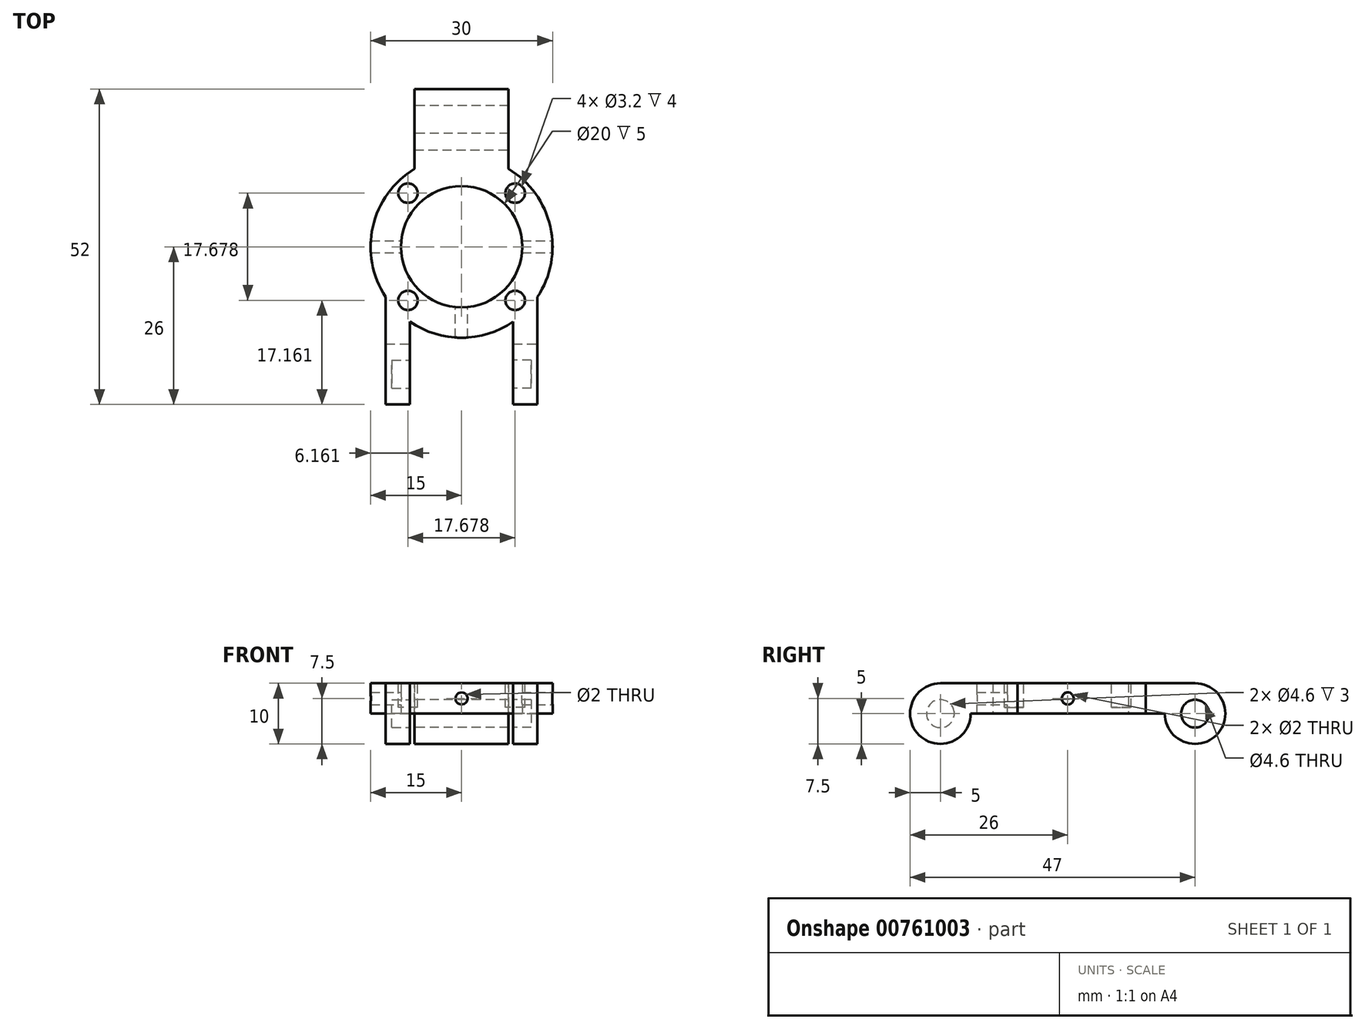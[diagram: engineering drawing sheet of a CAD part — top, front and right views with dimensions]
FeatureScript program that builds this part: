
annotation { "Feature Type Name" : "Feature", "Feature Type Description" : "" }
export const myFeature = defineFeature(function(context is Context, id is Id, definition is map)
    precondition{}
    {
        {
            var Q0;
            Q0=qCreatedBy(makeId("Top.planeOp"),FACE);
            var sketch = newSketch(context, id + "F0", { "sketchPlane" : qUnion([Q0])});
            skCircle(sketch, "E0", {"center": v(0, 0) * mm, "radius": 10 * mm});
            skArc(sketch, "E1", {"start": v(-7.75, 12.84) * mm, "mid": v(-15, 0.45) * mm, "end": v(-8.5, -12.36) * mm});
            skLineSegment(sketch, "E2", {"start": v(-7.75, 26) * mm, "end": v(-7.75, 12.84) * mm});
            skLineSegment(sketch, "E3", {"start": v(7.75, 26) * mm, "end": v(7.75, 12.84) * mm});
            skLineSegment(sketch, "E4", {"start": v(-7.75, 26) * mm, "end": v(7.75, 26) * mm});
            skLineSegment(sketch, "E5", {"start": v(-8.5, -12.36) * mm, "end": v(-8.5, -26) * mm});
            skLineSegment(sketch, "E6", {"start": v(8.5, -26) * mm, "end": v(8.5, -12.36) * mm});
            skArc(sketch, "E7.trimOffspring", {"start": v(8.5, -12.36) * mm, "mid": v(15, 0.45) * mm, "end": v(7.75, 12.84) * mm});
            skLineSegment(sketch, "E8", {"start": v(8.5, -26) * mm, "end": v(12.5, -26) * mm});
            skLineSegment(sketch, "E9", {"start": v(12.5, -26) * mm, "end": v(12.5, -8.3) * mm});
            skLineSegment(sketch, "E10", {"start": v(-8.5, -26) * mm, "end": v(-12.5, -26) * mm});
            skLineSegment(sketch, "E11", {"start": v(-12.5, -26) * mm, "end": v(-12.5, -8.3) * mm});
            skCircle(sketch, "E12", {"center": v(0, 0) * mm, "radius": 15 * mm});
            skPoint(sketch, "E13.orphan", {"position": v(7.75, 6.32) * mm});
            skSolve(sketch);
        }
        {
            var Q0;
            Q0 = qSketchRegion(id + "F0", true);
            extrude(context, id + "F1", {"entities" : qUnion([Q0]), "depth" : 5 * mm, "offsetDistance" : 25 * mm});
        }
        {
            var Q0;
            Q0=makeQuery(id+"F1.opExtrude","CAP_FACE",FACE,{"disambiguationData":[OSD([sQuery(id+"F0.wireOp",EDGE,"E0"),sQuery(id+"F0.wireOp",EDGE,"E1"),sQuery(id+"F0.wireOp",EDGE,"E2"),sQuery(id+"F0.wireOp",EDGE,"E3"),sQuery(id+"F0.wireOp",EDGE,"E4")])],"isStart":true});
            var sketch = newSketch(context, id + "F2", { "sketchPlane" : qUnion([Q0])});
            skLineSegment(sketch, "E14.0", {"start": v(7.75, -26) * mm, "end": v(7.75, -16) * mm});
            skLineSegment(sketch, "E14.1", {"start": v(-7.75, -26) * mm, "end": v(7.75, -26) * mm});
            skLineSegment(sketch, "E14.2", {"start": v(-7.75, -26) * mm, "end": v(-7.75, -16) * mm});
            skLineSegment(sketch, "E15", {"start": v(-7.75, -16) * mm, "end": v(7.75, -16) * mm});
            skLineSegment(sketch, "E16.bottom", {"start": v(-12.5, 26) * mm, "end": v(-8.5, 26) * mm});
            skLineSegment(sketch, "E16.top", {"start": v(-12.5, 16) * mm, "end": v(-8.5, 16) * mm});
            skLineSegment(sketch, "E16.left", {"start": v(-12.5, 26) * mm, "end": v(-12.5, 16) * mm});
            skLineSegment(sketch, "E16.right", {"start": v(-8.5, 26) * mm, "end": v(-8.5, 16) * mm});
            skLineSegment(sketch, "E17.bottom", {"start": v(8.5, 26) * mm, "end": v(12.5, 26) * mm});
            skLineSegment(sketch, "E17.top", {"start": v(8.5, 16) * mm, "end": v(12.5, 16) * mm});
            skLineSegment(sketch, "E17.left", {"start": v(8.5, 26) * mm, "end": v(8.5, 16) * mm});
            skLineSegment(sketch, "E17.right", {"start": v(12.5, 26) * mm, "end": v(12.5, 16) * mm});
            skSolve(sketch);
        }
        {
            var Q0;
            Q0 = qSketchRegion(id + "F2", true);
            extrude(context, id + "F3", {"entities" : qUnion([Q0]), "operationType" : NewBodyOperationType.ADD, "depth" : 5 * mm, "offsetDistance" : 25 * mm});
        }
        {
            var Q0;
            Q0=makeQuery(id+"F3.boolean.opBoolean","MERGE",FACE,{"derivedFrom":[makeQuery(id+"F1.opExtrude","SWEPT_FACE",FACE,{"disambiguationData":[OSD([sQuery(id+"F0.wireOp",EDGE,"E2")])]}),makeQuery(id+"F3.opExtrude","SWEPT_FACE",FACE,{"disambiguationData":[OSD([sQuery(id+"F2.wireOp",EDGE,"E14.2")])]})]});
            var sketch = newSketch(context, id + "F4", { "sketchPlane" : qUnion([Q0])});
            skCircle(sketch, "E18", {"center": v(-21, 0) * mm, "radius": 2.3 * mm});
            skSolve(sketch);
        }
        {
            var Q0;
            Q0 = qSketchRegion(id + "F4", true);
            extrude(context, id + "F5", {"entities" : qUnion([Q0]), "operationType" : NewBodyOperationType.REMOVE, "endBound" : BoundingType.THROUGH_ALL, "oppositeDirection" : true, "depth" : 25 * mm, "offsetDistance" : 25 * mm});
        }
        {
            var Q0;
            Q0=makeQuery(id+"F1.opExtrude","CAP_FACE",FACE,{"disambiguationData":[OSD([sQuery(id+"F0.wireOp",EDGE,"E0"),sQuery(id+"F0.wireOp",EDGE,"E1"),sQuery(id+"F0.wireOp",EDGE,"E2"),sQuery(id+"F0.wireOp",EDGE,"E3"),sQuery(id+"F0.wireOp",EDGE,"E4")])],"isStart":false});
            var sketch = newSketch(context, id + "F6", { "sketchPlane" : qUnion([Q0])});
            skLineSegment(sketch, "E19", {"start": v(0, 0) * mm, "end": v(21.62, -21.62) * mm});
            skLineSegment(sketch, "E20", {"start": v(0, 0) * mm, "end": v(22.98, 22.98) * mm});
            skLineSegment(sketch, "E21", {"start": v(0, 0) * mm, "end": v(-21.47, 21.47) * mm});
            skLineSegment(sketch, "E22", {"start": v(0, 0) * mm, "end": v(-23.27, -23.27) * mm});
            skCircle(sketch, "E23", {"center": v(8.84, 8.84) * mm, "radius": 1.6 * mm});
            skCircle(sketch, "E24", {"center": v(8.84, -8.84) * mm, "radius": 1.6 * mm});
            skCircle(sketch, "E25", {"center": v(-8.84, -8.84) * mm, "radius": 1.6 * mm});
            skCircle(sketch, "E26", {"center": v(-8.84, 8.84) * mm, "radius": 1.6 * mm});
            skSolve(sketch);
        }
        {
            var Q0;
            Q0 = qSketchRegion(id + "F6", true);
            extrude(context, id + "F7", {"entities" : qUnion([Q0]), "operationType" : NewBodyOperationType.REMOVE, "oppositeDirection" : true, "depth" : 4 * mm, "offsetDistance" : 25 * mm});
        }
        {
            var Q0;
            Q0=makeQuery(id+"F3.boolean.opBoolean","MERGE",FACE,{"derivedFrom":[makeQuery(id+"F1.opExtrude","SWEPT_FACE",FACE,{"disambiguationData":[OSD([sQuery(id+"F0.wireOp",EDGE,"E5")])]}),makeQuery(id+"F3.opExtrude","SWEPT_FACE",FACE,{"disambiguationData":[OSD([sQuery(id+"F2.wireOp",EDGE,"E16.right")])]})]});
            var sketch = newSketch(context, id + "F8", { "sketchPlane" : qUnion([Q0])});
            skCircle(sketch, "E27", {"center": v(-21, 0) * mm, "radius": 2.3 * mm});
            skSolve(sketch);
        }
        {
            var Q0;
            Q0 = qSketchRegion(id + "F8", true);
            extrude(context, id + "F9", {"entities" : qUnion([Q0]), "operationType" : NewBodyOperationType.REMOVE, "oppositeDirection" : true, "depth" : 3 * mm, "offsetDistance" : 25 * mm});
        }
        {
            var Q0;
            Q0=makeQuery(id+"F3.boolean.opBoolean","MERGE",FACE,{"derivedFrom":[makeQuery(id+"F1.opExtrude","SWEPT_FACE",FACE,{"disambiguationData":[OSD([sQuery(id+"F0.wireOp",EDGE,"E6")])]}),makeQuery(id+"F3.opExtrude","SWEPT_FACE",FACE,{"disambiguationData":[OSD([sQuery(id+"F2.wireOp",EDGE,"E17.left")])]})]});
            var sketch = newSketch(context, id + "F10", { "sketchPlane" : qUnion([Q0])});
            skCircle(sketch, "E28", {"center": v(21, 0) * mm, "radius": 2.3 * mm});
            skSolve(sketch);
        }
        {
            var Q0;
            Q0 = qSketchRegion(id + "F10", true);
            extrude(context, id + "F11", {"entities" : qUnion([Q0]), "operationType" : NewBodyOperationType.REMOVE, "oppositeDirection" : true, "depth" : 3 * mm, "offsetDistance" : 25 * mm});
        }
        {
            var Q0;
            Q0=makeQuery(id+"F3.opExtrude","CAP_EDGE",EDGE,{"disambiguationData":[OSD([sQuery(id+"F2.wireOp",EDGE,"E14.1")])],"isStart":false});
            var Q1;
            Q1=makeQuery(id+"F3.opExtrude","CAP_EDGE",EDGE,{"disambiguationData":[OSD([sQuery(id+"F2.wireOp",EDGE,"E15")])],"isStart":false});
            var Q2;
            Q2=makeQuery(id+"F1.opExtrude","CAP_EDGE",EDGE,{"disambiguationData":[OSD([sQuery(id+"F0.wireOp",EDGE,"E4")])],"isStart":false});
            var Q3;
            Q3=makeQuery(id+"F3.opExtrude","CAP_EDGE",EDGE,{"disambiguationData":[OSD([sQuery(id+"F2.wireOp",EDGE,"E16.bottom")])],"isStart":false});
            var Q4;
            Q4=makeQuery(id+"F1.opExtrude","CAP_EDGE",EDGE,{"disambiguationData":[OSD([sQuery(id+"F0.wireOp",EDGE,"E10")])],"isStart":false});
            var Q5;
            Q5=makeQuery(id+"F1.opExtrude","CAP_EDGE",EDGE,{"disambiguationData":[OSD([sQuery(id+"F0.wireOp",EDGE,"E8")])],"isStart":false});
            var Q6;
            Q6=makeQuery(id+"F3.opExtrude","CAP_EDGE",EDGE,{"disambiguationData":[OSD([sQuery(id+"F2.wireOp",EDGE,"E17.bottom")])],"isStart":false});
            var Q7;
            Q7=makeQuery(id+"F3.opExtrude","CAP_EDGE",EDGE,{"disambiguationData":[OSD([sQuery(id+"F2.wireOp",EDGE,"E16.top")])],"isStart":false});
            var Q8;
            Q8=makeQuery(id+"F3.opExtrude","CAP_EDGE",EDGE,{"disambiguationData":[OSD([sQuery(id+"F2.wireOp",EDGE,"E17.top")])],"isStart":false});
            fillet(context, id + "F12", {"entities" : qUnion([Q0, Q1, Q2, Q3, Q4, Q5, Q6, Q7, Q8]), "radius" : 5 * mm, "tangentPropagation" : true, "allowEdgeOverflow" : false});
        }
        {
            var Q0;
            Q0=qCreatedBy(makeId("Right.planeOp"),FACE);
            var sketch = newSketch(context, id + "F13", { "sketchPlane" : qUnion([Q0])});
            skCircle(sketch, "E29", {"center": v(0, 2.5) * mm, "radius": 1 * mm});
            skSolve(sketch);
        }
        {
            var Q0;
            Q0 = qSketchRegion(id + "F13", true);
            extrude(context, id + "F14", {"entities" : qUnion([Q0]), "operationType" : NewBodyOperationType.REMOVE, "endBound" : BoundingType.SYMMETRIC, "oppositeDirection" : true, "depth" : 50 * mm, "offsetDistance" : 25 * mm});
        }
        {
            var Q0;
            Q0=qCreatedBy(makeId("Front.planeOp"),FACE);
            var sketch = newSketch(context, id + "F15", { "sketchPlane" : qUnion([Q0])});
            skCircle(sketch, "E30", {"center": v(0, 2.5) * mm, "radius": 1 * mm});
            skSolve(sketch);
        }
        {
            var Q0;
            Q0 = qSketchRegion(id + "F15", true);
            extrude(context, id + "F16", {"entities" : qUnion([Q0]), "operationType" : NewBodyOperationType.REMOVE, "depth" : 25 * mm, "offsetDistance" : 25 * mm});
        }
    });
